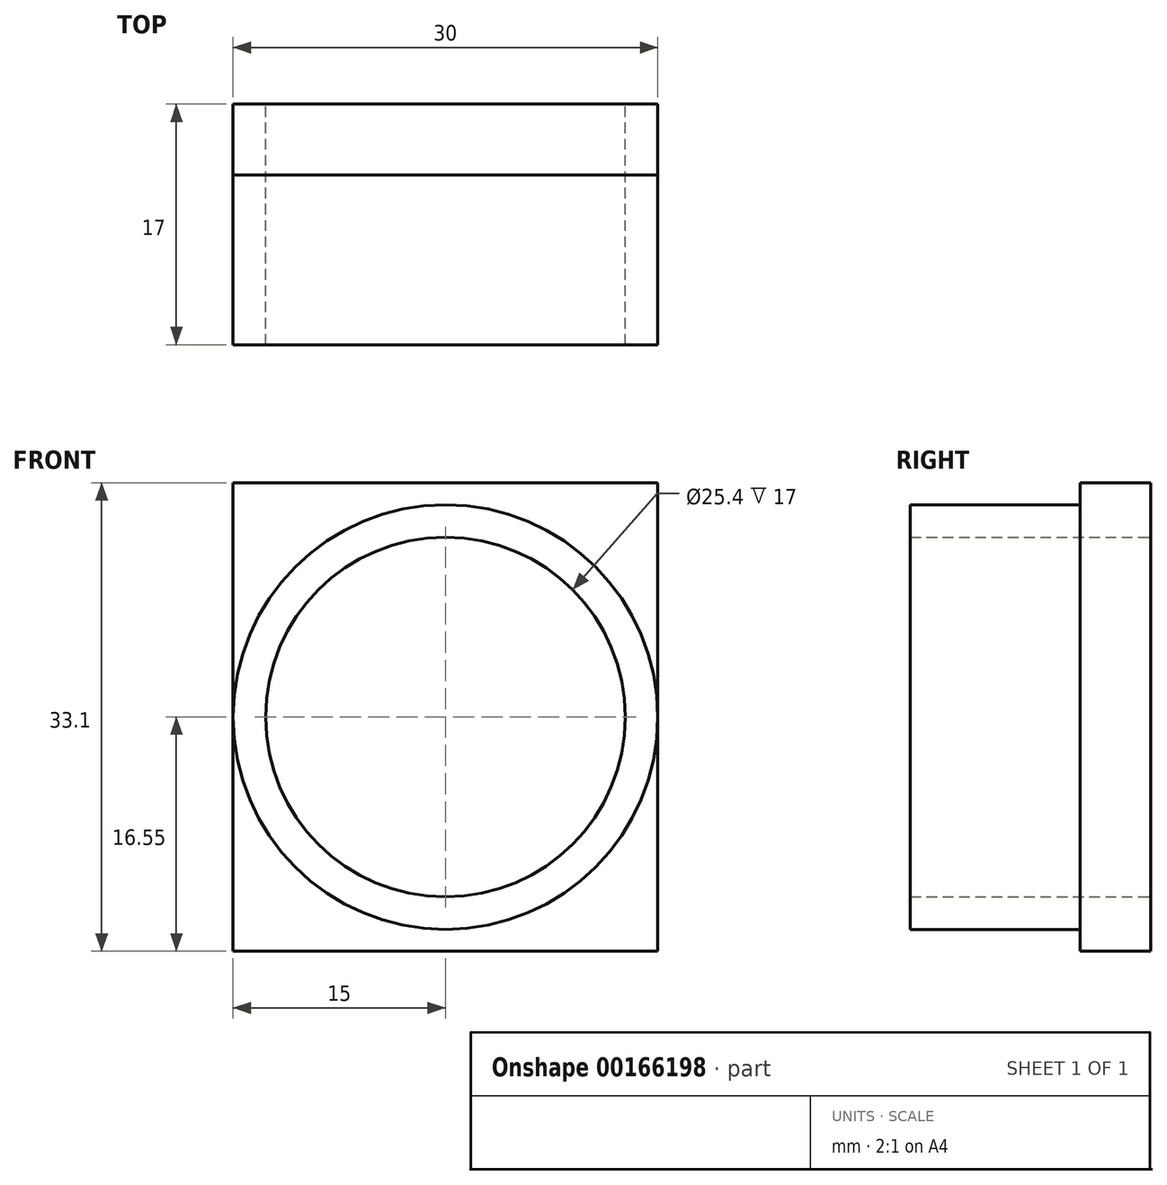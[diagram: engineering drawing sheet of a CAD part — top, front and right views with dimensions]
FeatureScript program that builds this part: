
annotation { "Feature Type Name" : "Feature", "Feature Type Description" : "" }
export const myFeature = defineFeature(function(context is Context, id is Id, definition is map)
    precondition{}
    {
        {
            var Q0;
            Q0=qCreatedBy(makeId("Front.planeOp"),FACE);
            var sketch = newSketch(context, id + "F0", { "sketchPlane" : qUnion([Q0])});
            skLineSegment(sketch, "E0.bottom", {"start": v(15, 16.55) * mm, "end": v(-15, 16.55) * mm});
            skLineSegment(sketch, "E0.top", {"start": v(15, -16.55) * mm, "end": v(-15, -16.55) * mm});
            skLineSegment(sketch, "E0.left", {"start": v(15, 16.55) * mm, "end": v(15, -16.55) * mm});
            skLineSegment(sketch, "E0.right", {"start": v(-15, 16.55) * mm, "end": v(-15, -16.55) * mm});
            skPoint(sketch, "E0.middle", {"position": v(0, 0) * mm});
            skSolve(sketch);
        }
        {
            var Q0;
            Q0 = qSketchRegion(id + "F0", true);
            extrude(context, id + "F1", {"entities" : qUnion([Q0]), "depth" : 5 * mm});
        }
        {
            var Q0;
            Q0=makeQuery(id+"F1.opExtrude","CAP_FACE",FACE,{"disambiguationData":[OSD([sQuery(id+"F0.wireOp",EDGE,"E0.bottom"),sQuery(id+"F0.wireOp",EDGE,"E0.top"),sQuery(id+"F0.wireOp",EDGE,"E0.left"),sQuery(id+"F0.wireOp",EDGE,"E0.right")])],"isStart":false});
            var sketch = newSketch(context, id + "F2", { "sketchPlane" : qUnion([Q0])});
            skCircle(sketch, "E1", {"center": v(0, 0) * mm, "radius": 15 * mm});
            skCircle(sketch, "E2", {"center": v(0, 0) * mm, "radius": 12.7 * mm});
            skSolve(sketch);
        }
        {
            var Q0;
            Q0 = qSketchRegion(id + "F2", true);
            extrude(context, id + "F3", {"entities" : qUnion([Q0]), "operationType" : NewBodyOperationType.ADD, "depth" : 12 * mm});
        }
        {
            var Q0;
            Q0=makeQuery(id+"F3.boolean.opBoolean","SPLIT",FACE,{"disambiguationData":[TD([makeQuery(id+"F3.opExtrude","SWEPT_FACE",FACE,{"disambiguationData":[OSD([sQuery(id+"F2.wireOp",EDGE,"E2")])]})])],"derivedFrom":makeQuery(id+"F1.opExtrude","CAP_FACE",FACE,{"disambiguationData":[OSD([sQuery(id+"F0.wireOp",EDGE,"E0.bottom"),sQuery(id+"F0.wireOp",EDGE,"E0.top"),sQuery(id+"F0.wireOp",EDGE,"E0.left"),sQuery(id+"F0.wireOp",EDGE,"E0.right")])],"isStart":false})});
            var sketch = newSketch(context, id + "F4", { "sketchPlane" : qUnion([Q0])});
            skCircle(sketch, "E3.0", {"center": v(0, 0) * mm, "radius": 12.7 * mm});
            skSolve(sketch);
        }
        {
            var Q0;
            Q0 = qSketchRegion(id + "F4", true);
            extrude(context, id + "F5", {"entities" : qUnion([Q0]), "operationType" : NewBodyOperationType.REMOVE, "oppositeDirection" : true, "depth" : 25 * mm});
        }
    });
